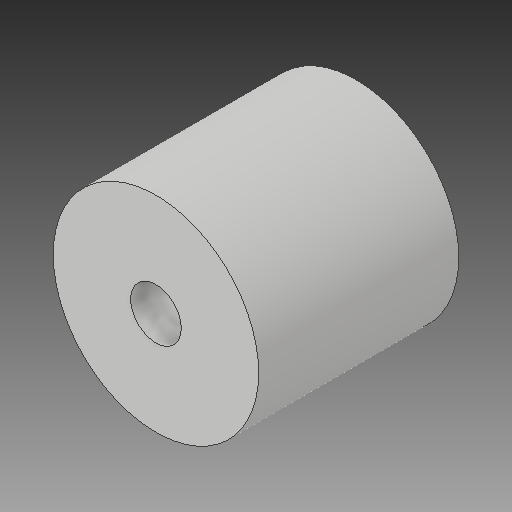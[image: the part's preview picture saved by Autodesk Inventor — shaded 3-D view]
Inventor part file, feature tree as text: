
AUTODESK INVENTOR PART (.ipt)
format: ipt  version: 2017 (Build 210142000, 142)  size: 108,032 bytes
history: native  units: in
note: dims shown in document units (in); Inventor stores cm internally (conversion verified against a paired STEP export)
features: chamfer x1
ambient origin geometry x8: Origin, YZ Plane, XZ Plane, XY Plane, X Axis, Y Axis, Z Axis, Center Point
bodies: Solid1 (feature_tree)
feature tree (1):
  chamfer  "Chamfer2"  [1 undecoded]
note: 1 required parameter value undecoded (feature->parameter linkage not recoverable at this tier; creation-order binding heuristic only, values carry confidence <= 0.55)
